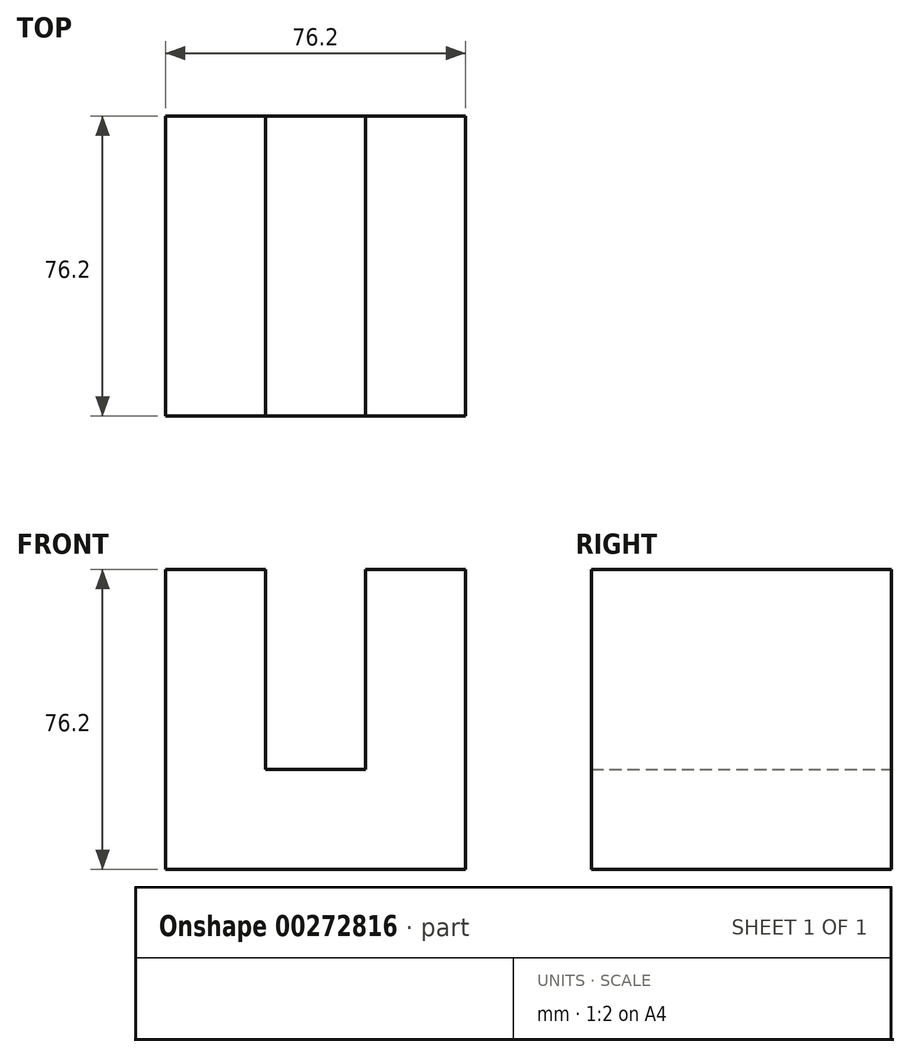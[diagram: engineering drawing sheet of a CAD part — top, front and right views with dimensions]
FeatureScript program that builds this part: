
annotation { "Feature Type Name" : "Feature", "Feature Type Description" : "" }
export const myFeature = defineFeature(function(context is Context, id is Id, definition is map)
    precondition{}
    {
        {
            var Q0;
            Q0=qCreatedBy(makeId("Front.planeOp"),FACE);
            var sketch = newSketch(context, id + "F0", { "sketchPlane" : qUnion([Q0])});
            skLineSegment(sketch, "E0", {"start": v(0, 0) * mm, "end": v(-76.2, 0) * mm});
            skLineSegment(sketch, "E1", {"start": v(-76.2, 0) * mm, "end": v(-76.2, 76.2) * mm});
            skLineSegment(sketch, "E2", {"start": v(-76.2, 76.2) * mm, "end": v(-50.8, 76.2) * mm});
            skLineSegment(sketch, "E3", {"start": v(-25.4, 76.2) * mm, "end": v(0, 76.2) * mm});
            skLineSegment(sketch, "E4", {"start": v(0, 76.2) * mm, "end": v(0, 0) * mm});
            skLineSegment(sketch, "E5", {"start": v(-50.8, 76.2) * mm, "end": v(-50.8, 25.4) * mm});
            skLineSegment(sketch, "E6", {"start": v(-50.8, 25.4) * mm, "end": v(-25.4, 25.4) * mm});
            skLineSegment(sketch, "E7", {"start": v(-25.4, 76.2) * mm, "end": v(-25.4, 25.4) * mm});
            skSolve(sketch);
        }
        {
            var Q0;
            Q0 = qSketchRegion(id + "F0", true);
            var Q1;
            Q1=makeQuery(id+"F0.imprint","IMPRINT",FACE,{"disambiguationData":[TD([[makeQuery(id+"F0.imprint","IMPRINT",EDGE,{"derivedFrom":sQuery(id+"F0.wireOp",EDGE,"E0")}),-1.0]])]});
            extrude(context, id + "F1", {"entities" : qUnion([Q0, Q1]), "depth" : 76.2 * mm});
        }
    });
